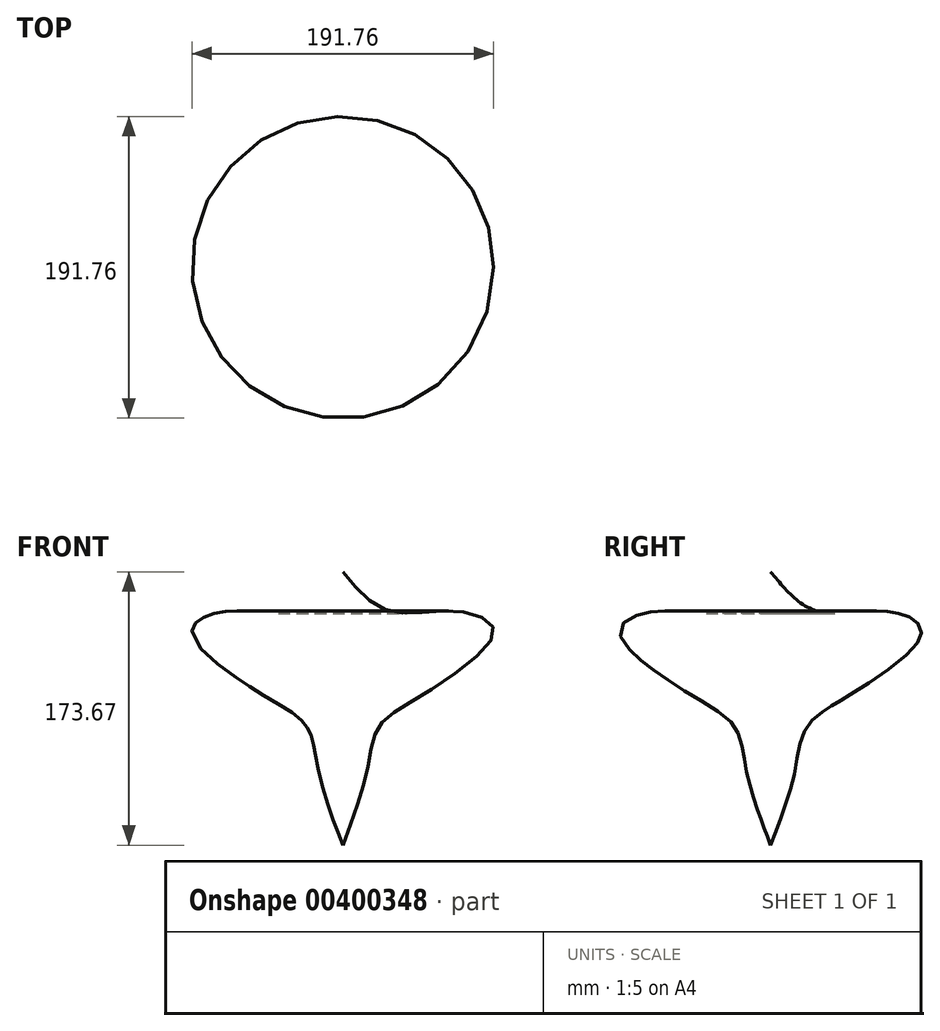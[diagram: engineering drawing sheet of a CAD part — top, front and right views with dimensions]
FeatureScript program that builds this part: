
annotation { "Feature Type Name" : "Feature", "Feature Type Description" : "" }
export const myFeature = defineFeature(function(context is Context, id is Id, definition is map)
    precondition{}
    {
        {
            var Q0;
            Q0=qCreatedBy(makeId("Front.planeOp"),FACE);
            var sketch = newSketch(context, id + "F0", { "sketchPlane" : qUnion([Q0])});
            skLineSegment(sketch, "E0", {"start": v(0, 86.96) * mm, "end": v(0, -86.71) * mm});
            skFitSpline(sketch, "E1", {"points": [v(0, 86.96) * mm, v(29.26, 62.02) * mm, v(72.61, 61.85) * mm, v(95.88, 48.83) * mm, v(49, 7.8) * mm, v(22.2, -12.62) * mm, v(15.16, -40.74) * mm, v(0, -86.71) * mm], "startDerivative": vector(186.77, -229.07) * mm, "endDerivative": vector(-114.88, -301.32) * mm});
            skSolve(sketch);
        }
        {
            var Q0;
            Q0=sQuery(id+"F0.wireOp",EDGE,"E1");
            var Q1;
            Q1=sQuery(id+"F0.wireOp",EDGE,"E0");
            revolve(context, id + "F1", {"bodyType" : ToolBodyType.SURFACE, "surfaceEntities" : qUnion([Q0]), "axis" : qUnion([Q1]), "revolveType" : RevolveType.FULL});
        }
    });
